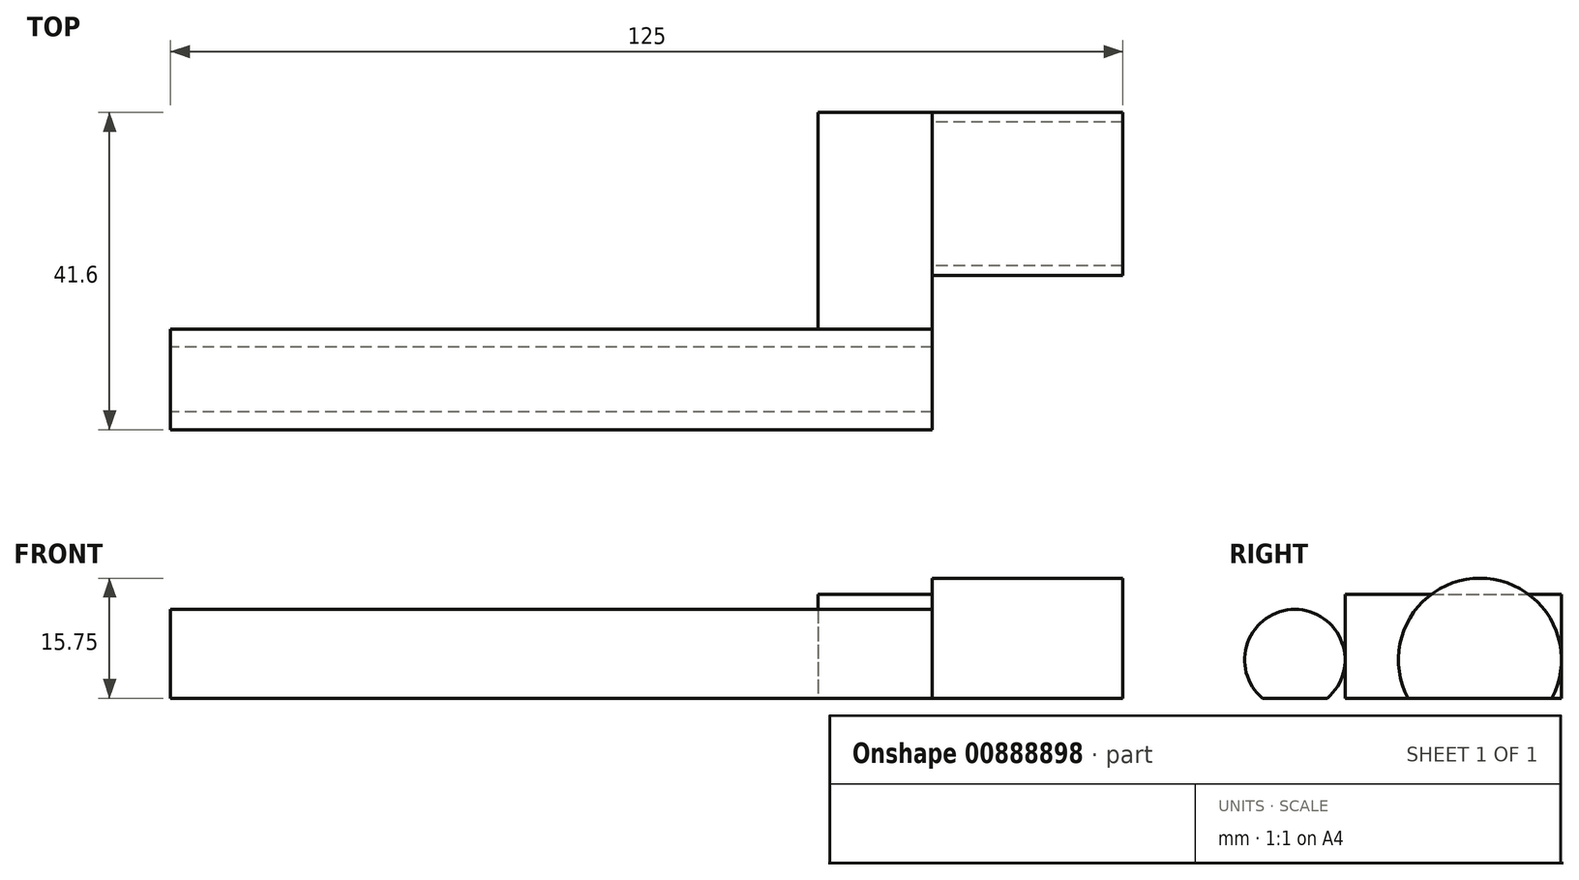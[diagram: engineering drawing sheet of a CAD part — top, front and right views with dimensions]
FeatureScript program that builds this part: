
annotation { "Feature Type Name" : "Feature", "Feature Type Description" : "" }
export const myFeature = defineFeature(function(context is Context, id is Id, definition is map)
    precondition{}
    {
        {
            var Q0;
            Q0=qCreatedBy(makeId("Top.planeOp"),FACE);
            var sketch = newSketch(context, id + "F0", { "sketchPlane" : qUnion([Q0])});
            skLineSegment(sketch, "E0.bottom", {"start": v(0, 0) * mm, "end": v(100, 0) * mm});
            skLineSegment(sketch, "E0.top", {"start": v(0, 6.6) * mm, "end": v(100, 6.6) * mm});
            skLineSegment(sketch, "E0.left", {"start": v(0, 0) * mm, "end": v(0, 6.6) * mm});
            skLineSegment(sketch, "E0.right", {"start": v(100, 0) * mm, "end": v(100, 6.6) * mm});
            skLineSegment(sketch, "E1.bottom", {"start": v(100, 0) * mm, "end": v(85, 0) * mm});
            skLineSegment(sketch, "E2.bottom", {"start": v(85, 0) * mm, "end": v(100, 0) * mm});
            skLineSegment(sketch, "E2.top", {"start": v(85, 35) * mm, "end": v(100, 35) * mm});
            skLineSegment(sketch, "E2.left", {"start": v(85, 0) * mm, "end": v(85, 35) * mm});
            skLineSegment(sketch, "E2.right", {"start": v(100, 0) * mm, "end": v(100, 35) * mm});
            skLineSegment(sketch, "E3", {"start": v(100, 35) * mm, "end": v(100, 24.3) * mm});
            skLineSegment(sketch, "E4.bottom", {"start": v(100, 35) * mm, "end": v(125, 35) * mm});
            skLineSegment(sketch, "E4.top", {"start": v(100, 24.3) * mm, "end": v(125, 24.3) * mm});
            skLineSegment(sketch, "E4.right", {"start": v(125, 35) * mm, "end": v(125, 24.3) * mm});
            skLineSegment(sketch, "E5.top", {"start": v(85, -6.5) * mm, "end": v(100, -6.5) * mm});
            skLineSegment(sketch, "E5.left", {"start": v(85, 0) * mm, "end": v(85, -6.5) * mm});
            skLineSegment(sketch, "E5.right", {"start": v(100, 0) * mm, "end": v(100, -6.5) * mm});
            skSolve(sketch);
        }
        {
            var Q0;
            {var subQ0=sQuery(id+"F0.wireOp",EDGE,"E0.bottom");Q0=makeQuery(id+"F0.imprint","IMPRINT",FACE,{"disambiguationData":[TD([[makeQuery(id+"F0.imprint","IMPRINT",EDGE,{"derivedFrom":subQ0}),1.0]])]});}
            var Q1;
            {var subQ5=sQuery(id+"F0.wireOp",EDGE,"E1.bottom");Q1=makeQuery(id+"F0.imprint","IMPRINT",FACE,{"disambiguationData":[TD([[makeQuery(id+"F0.imprint","IMPRINT",EDGE,{"derivedFrom":subQ5}),-1.0]])]});}
            var Q2;
            Q2=sQuery(id+"F0.wireOp",EDGE,"E0.bottom");
            revolve(context, id + "F1", {"surfaceOperationType" : NewSurfaceOperationType.NEW, "entities" : qUnion([Q0, Q1]), "axis" : qUnion([Q2]), "revolveType" : RevolveType.FULL});
        }
        {
            var Q0;
            Q0=makeQuery(id+"F0.imprint","IMPRINT",FACE,{"disambiguationData":[TD([[makeQuery(id+"F0.imprint","IMPRINT",EDGE,{"derivedFrom":sQuery(id+"F0.wireOp",EDGE,"E4.bottom")}),-1.0]])]});
            var Q1;
            Q1=sQuery(id+"F0.wireOp",EDGE,"E4.top");
            revolve(context, id + "F2", {"surfaceOperationType" : NewSurfaceOperationType.NEW, "entities" : qUnion([Q0]), "axis" : qUnion([Q1]), "revolveType" : RevolveType.FULL});
        }
        {
            var Q0;
            {var subQ4=sQuery(id+"F0.wireOp",EDGE,"E2.top");Q0=makeQuery(id+"F0.imprint","IMPRINT",FACE,{"disambiguationData":[TD([[makeQuery(id+"F0.imprint","IMPRINT",EDGE,{"derivedFrom":subQ4}),-1.0]])]});}
            var Q1;
            {var subQ5=sQuery(id+"F0.wireOp",EDGE,"E2.bottom");Q1=makeQuery(id+"F0.imprint","IMPRINT",FACE,{"disambiguationData":[TD([[makeQuery(id+"F0.imprint","IMPRINT",EDGE,{"derivedFrom":subQ5}),1.0]])]});}
            var Q2;
            Q2=makeQuery(id+"F0.imprint","IMPRINT",FACE,{"disambiguationData":[TD([[makeQuery(id+"F0.imprint","IMPRINT",EDGE,{"derivedFrom":sQuery(id+"F0.wireOp",EDGE,"E2.bottom")}),-1.0]])]});
            var Q3;
            {var subQ5=sQuery(id+"F0.wireOp",EDGE,"E2.bottom");Q3=makeQuery(id+"F0.imprint","IMPRINT",FACE,{"disambiguationData":[TD([[makeQuery(id+"F0.imprint","IMPRINT",EDGE,{"derivedFrom":subQ5}),1.0]])]});}
            extrude(context, id + "F3", {"entities" : qUnion([Q0, Q1, Q2, Q3]), "endBound" : BoundingType.SYMMETRIC, "depth" : 17.1 * mm, "offsetDistance" : 25 * mm});
        }
        {
            var Q0;
            Q0=makeQuery(id+"F3.opExtrude","CAP_FACE",FACE,{"disambiguationData":[OSD([sQuery(id+"F0.wireOp",EDGE,"E2.bottom"),sQuery(id+"F0.wireOp",EDGE,"E2.top"),sQuery(id+"F0.wireOp",EDGE,"E2.left"),sQuery(id+"F0.wireOp",EDGE,"E2.right"),sQuery(id+"F0.wireOp",EDGE,"E3")])],"isStart":true});
            var sketch = newSketch(context, id + "F4", { "sketchPlane" : qUnion([Q0])});
            skLineSegment(sketch, "E6.bottom", {"start": v(148.12, 16.85) * mm, "end": v(-24.38, 16.85) * mm});
            skLineSegment(sketch, "E6.top", {"start": v(148.12, -62.94) * mm, "end": v(-24.38, -62.94) * mm});
            skLineSegment(sketch, "E6.left", {"start": v(148.12, 16.85) * mm, "end": v(148.12, -62.94) * mm});
            skLineSegment(sketch, "E6.right", {"start": v(-24.38, 16.85) * mm, "end": v(-24.38, -62.94) * mm});
            skSolve(sketch);
        }
        {
            var Q0;
            Q0 = qSketchRegion(id + "F4", true);
            extrude(context, id + "F5", {"entities" : qUnion([Q0]), "operationType" : NewBodyOperationType.REMOVE, "endBound" : BoundingType.SYMMETRIC, "oppositeDirection" : true, "depth" : 7 * mm, "offsetDistance" : 25 * mm});
        }
    });
